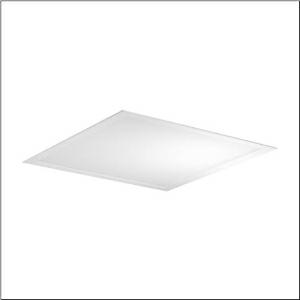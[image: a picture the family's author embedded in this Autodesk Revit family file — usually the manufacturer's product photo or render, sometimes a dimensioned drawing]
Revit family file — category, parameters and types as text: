
# Revit family: apollon_r__31_square_51mp11w72342_58c9
name_source: partatom
category: Lighting Fixtures
units: mm (PartAtom-declared; Revit-internal decimal feet)

## family parameters
Cut with Voids When Loaded = No
Host = Face
Light Source = No
Part Type = Normal
Room Calculation Point = No
Round Connector Dimension = Use Diameter
Shared = No

## types (1)
- Apollon® 31 square (1 x LED, 3800 lm, 27.5 W, 3000K)
    Apparent Load = 28 VA
    CIE Flux Codes = 61 87 97 100 100
    Color Rendering = 80
    Color Temperature = 3000K
    Default Elevation = 1800 mm
    Description = Apollon® 31 square, office luminaire, primary optical cover: micro prismatic cover, of PMMA, CAT 2 (L<= 3000cd/m²), light emission: direct distribution, primary light characteristic: symmetric, installation type: lay-in mounting, LED, rated luminous flux: 3.800lm, luminous efficacy: 138lm/W, light colour: 830, colour temperature: 3000K, control gear: ON/OFF, with terminal, 3-pole, mains connection: 220..240V, AC, 50/60Hz, rated input power: 28W, housing, of aluminium, traffic white (RAL 9016), module: M625, length: 620mm, width: 620mm, height: 62mm, recess depth: 180mm, housing upper side, of sheet steel, coated, protection rating (complete): IP20, protection rating (on room side): IP40, insulation class (complete): insulation class II (safety insulation), certification: CE, ENEC, impact resistance: IK03, permissible operating ambient temperature: -20..+40°C, permissible storage temperature: -20..+60°C, packaging unit: 1 piece
    Height = 0 mm  [stored 0 ft]
    Lamp = 1 x LED
    Lamp Light Flux = 3800 lm
    Lamp Power = 27.5 W
    Lamp count = 1
    Length = 620 mm
    Luminous efficacy = 138 lm/W
    Manufacturer = Siteco
    ModVariant = No
    Model = 51MP11W72342
    Mounting Place = Ceiling
    Mounting Type = Recessed
    Number of Poles = 1
    OnlyDefault = Yes
    Power Factor = 1
    Product Name = Apollon® 31 square
    Product group = office luminaire | ceiling recessed
    ProductGroupID = 401
    Protection Class = Protection class II
    Protection Degree = IP 20
    RLX_Detail_Level = 1
    RLX_Emergency_Light_Flux = 0 lm
    RLX_Emergency_Type = 0
    RLX_Emergency_Type_DB = No
    RlxData = <blob elided: 12977 chars, md5=e4f7a921>
    Socket = socket
    Standby Power = 0 W
    System Light Flux = 3800 lm
    System Power = 28 W
    Type Comments = Product without accessories
    Type Image = l_1291039.jpg
    URL = http://relux.com
    VarID = ---
    Voltage = 0 V
    Weight = 0.00 kg
    Width = 620 mm

note: [stored X ft] marks values corroborated as IEEE doubles in the binary element streams (Revit-internal decimal feet)

## geometry (parser evidence)
native form markers: Sweep x8
no freeform markers — native parametric forms only
